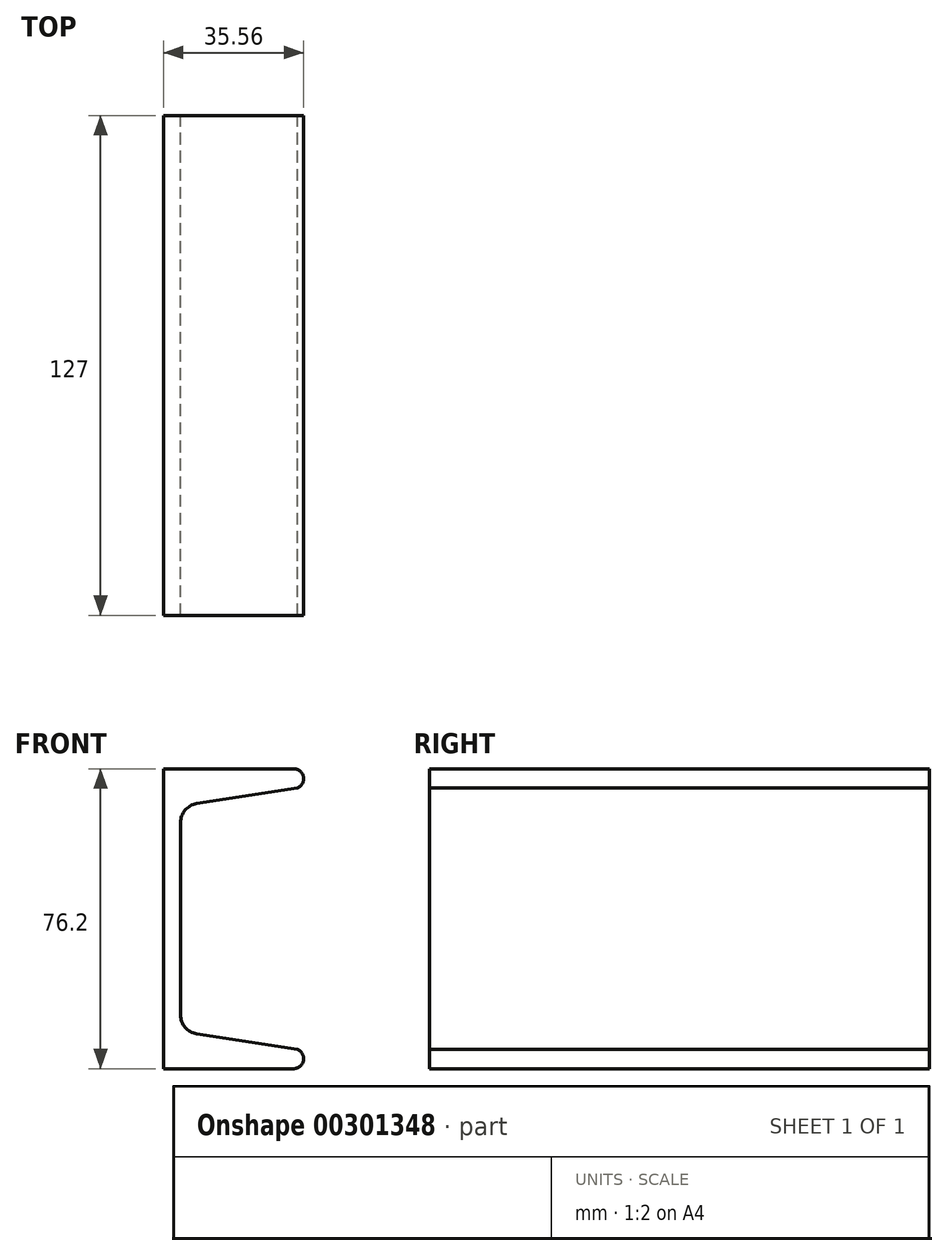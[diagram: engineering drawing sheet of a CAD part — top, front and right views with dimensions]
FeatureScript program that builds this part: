
annotation { "Feature Type Name" : "Feature", "Feature Type Description" : "" }
export const myFeature = defineFeature(function(context is Context, id is Id, definition is map)
    precondition{}
    {
        {
            var Q0;
            Q0=qCreatedBy(makeId("Front.planeOp"),FACE);
            var sketch = newSketch(context, id + "F0", { "sketchPlane" : qUnion([Q0])});
            skLineSegment(sketch, "E0", {"start": v(0, 38.1) * mm, "end": v(0, 0) * mm});
            skLineSegment(sketch, "E1", {"start": v(0, 38.1) * mm, "end": v(33.02, 38.1) * mm});
            skArc(sketch, "E2", {"start": v(33.02, 38.1) * mm, "mid": v(35.56, 35.41) * mm, "end": v(32.72, 33.04) * mm});
            skLineSegment(sketch, "E3", {"start": v(4.32, 24.44) * mm, "end": v(4.32, 0) * mm});
            skArc(sketch, "E4", {"start": v(4.32, 24.44) * mm, "mid": v(5.48, 27.6) * mm, "end": v(8.42, 29.24) * mm});
            skLineSegment(sketch, "E5", {"start": v(8.42, 29.24) * mm, "end": v(34.07, 33.25) * mm});
            skPoint(sketch, "E6.orphan", {"position": v(65.1, 38.1) * mm});
            skLineSegment(sketch, "E7.MirrorCS", {"start": v(0, -38.1) * mm, "end": v(33.02, -38.1) * mm});
            skArc(sketch, "E8.MirrorCS", {"start": v(33.02, -38.1) * mm, "mid": v(35.56, -35.41) * mm, "end": v(32.72, -33.04) * mm});
            skLineSegment(sketch, "E9.MirrorCS", {"start": v(8.42, -29.24) * mm, "end": v(34.07, -33.25) * mm});
            skLineSegment(sketch, "E10.MirrorCS", {"start": v(4.32, -24.44) * mm, "end": v(4.32, 0) * mm});
            skLineSegment(sketch, "E11.MirrorCS", {"start": v(0, -38.1) * mm, "end": v(0, 0) * mm});
            skArc(sketch, "E12.MirrorCS", {"start": v(4.32, -24.44) * mm, "mid": v(5.48, -27.6) * mm, "end": v(8.42, -29.24) * mm});
            skSolve(sketch);
        }
        {
            var Q0;
            Q0=makeQuery(id+"F0.imprint","IMPRINT",FACE,{"disambiguationData":[TD([[makeQuery(id+"F0.imprint","IMPRINT",EDGE,{"derivedFrom":sQuery(id+"F0.wireOp",EDGE,"E0")}),1.0]])]});
            extrude(context, id + "F1", {"entities" : qUnion([Q0]), "endBound" : BoundingType.SYMMETRIC, "depth" : 127 * mm});
        }
    });
